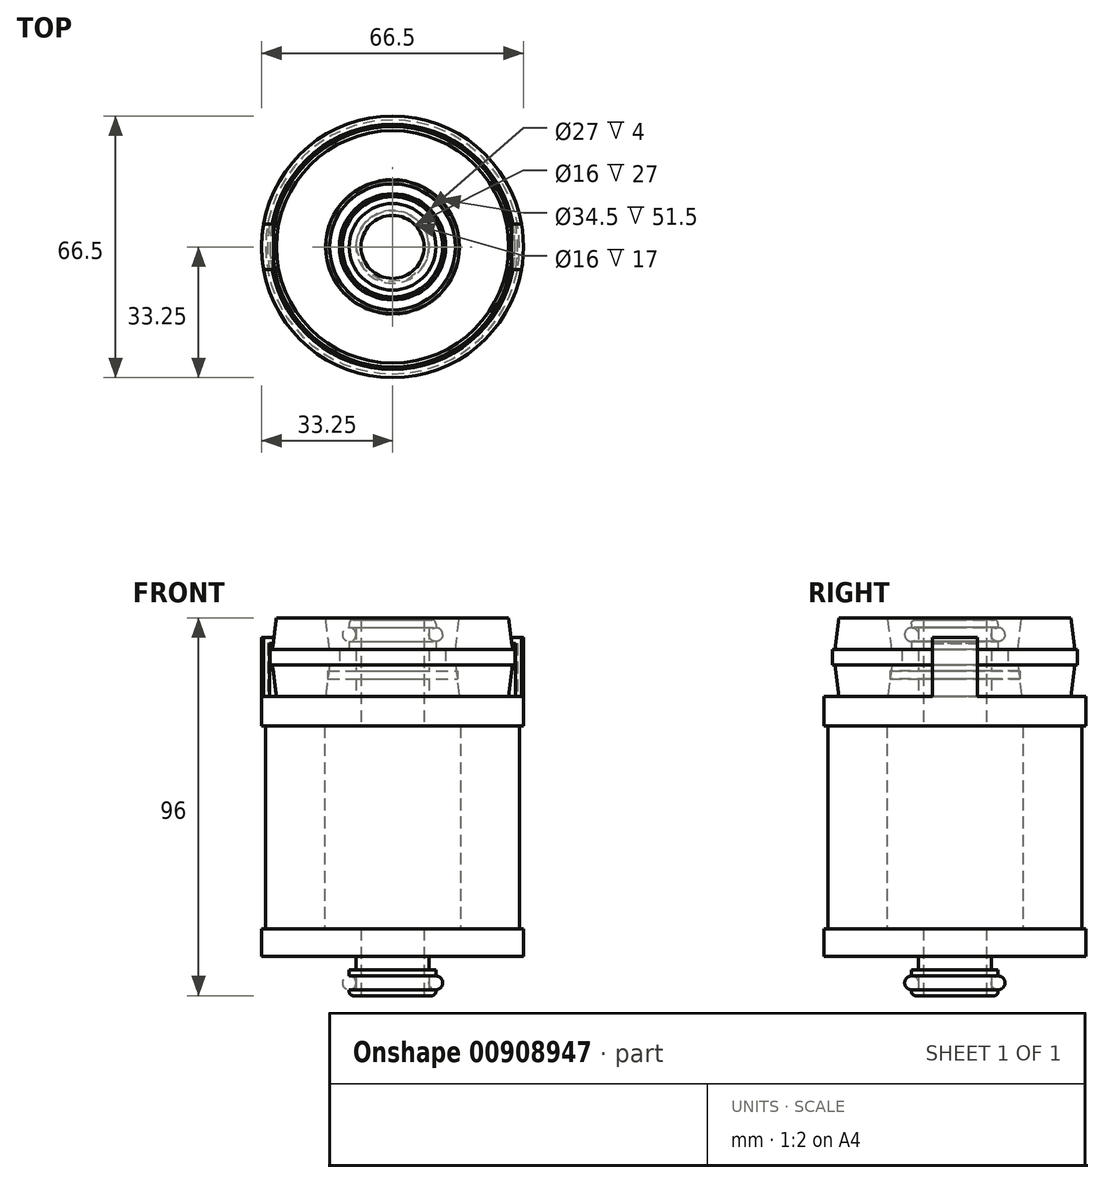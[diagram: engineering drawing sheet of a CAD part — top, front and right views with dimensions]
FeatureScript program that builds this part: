
annotation { "Feature Type Name" : "Feature", "Feature Type Description" : "" }
export const myFeature = defineFeature(function(context is Context, id is Id, definition is map)
    precondition{}
    {
        {
            var Q0;
            Q0=qCreatedBy(makeId("Front.planeOp"),FACE);
            var sketch = newSketch(context, id + "F0", { "sketchPlane" : qUnion([Q0])});
            skLineSegment(sketch, "E0", {"start": v(0, -41.92) * mm, "end": v(0, 59.56) * mm, "construction": true});
            skLineSegment(sketch, "E1", {"start": v(8, 0) * mm, "end": v(10, 0) * mm});
            skLineSegment(sketch, "E2", {"start": v(11, 1) * mm, "end": v(11, 1.5) * mm});
            skLineSegment(sketch, "E3", {"start": v(11, 1.5) * mm, "end": v(9.25, 1.5) * mm});
            skLineSegment(sketch, "E4", {"start": v(9.25, 1.5) * mm, "end": v(9.25, 5) * mm});
            skLineSegment(sketch, "E5", {"start": v(9.25, 5) * mm, "end": v(11, 5) * mm});
            skLineSegment(sketch, "E6", {"start": v(11, 5) * mm, "end": v(11, 6.5) * mm});
            skLineSegment(sketch, "E7", {"start": v(11, 6.5) * mm, "end": v(9.25, 6.5) * mm});
            skLineSegment(sketch, "E8", {"start": v(9.25, 6.5) * mm, "end": v(9.25, 10) * mm});
            skLineSegment(sketch, "E9", {"start": v(9.25, 10) * mm, "end": v(33.25, 10) * mm});
            skLineSegment(sketch, "E10", {"start": v(33.25, 10) * mm, "end": v(33.25, 17) * mm});
            skLineSegment(sketch, "E11", {"start": v(33.25, 76) * mm, "end": v(16.5, 76) * mm});
            skLineSegment(sketch, "E12", {"start": v(16.5, 80.5) * mm, "end": v(16.5, 82.5) * mm});
            skLineSegment(sketch, "E13", {"start": v(16.5, 82.5) * mm, "end": v(13.13, 82.5) * mm});
            skLineSegment(sketch, "E14", {"start": v(13.13, 82.5) * mm, "end": v(9.25, 82.5) * mm});
            skLineSegment(sketch, "E15", {"start": v(9.25, 82.5) * mm, "end": v(9.25, 88) * mm});
            skLineSegment(sketch, "E16", {"start": v(9.25, 88) * mm, "end": v(11, 88) * mm});
            skLineSegment(sketch, "E17", {"start": v(11, 88) * mm, "end": v(11, 90) * mm});
            skLineSegment(sketch, "E18", {"start": v(11, 90) * mm, "end": v(9.25, 90) * mm});
            skLineSegment(sketch, "E19", {"start": v(9.25, 90) * mm, "end": v(9.25, 93.5) * mm});
            skLineSegment(sketch, "E20", {"start": v(9.25, 93.5) * mm, "end": v(11, 93.5) * mm});
            skLineSegment(sketch, "E21", {"start": v(11, 93.5) * mm, "end": v(11, 94.5) * mm});
            skLineSegment(sketch, "E22", {"start": v(10, 95.5) * mm, "end": v(8, 95.5) * mm});
            skLineSegment(sketch, "E23", {"start": v(8, 95.5) * mm, "end": v(8, 68.5) * mm});
            skLineSegment(sketch, "E24", {"start": v(8, 68.5) * mm, "end": v(33.25, 68.5) * mm});
            skLineSegment(sketch, "E25", {"start": v(8, 0) * mm, "end": v(8, 17) * mm});
            skLineSegment(sketch, "E26", {"start": v(8, 17) * mm, "end": v(33.25, 17) * mm});
            skLineSegment(sketch, "E27", {"start": v(17.25, 17) * mm, "end": v(17.25, 68.5) * mm});
            skLineSegment(sketch, "E28", {"start": v(32.25, 68.5) * mm, "end": v(32.25, 17) * mm});
            skLineSegment(sketch, "E29.trimOffspring", {"start": v(33.25, 68.5) * mm, "end": v(33.25, 76) * mm});
            skLineSegment(sketch, "E30", {"start": v(16.5, 76) * mm, "end": v(9.25, 76) * mm});
            skLineSegment(sketch, "E31", {"start": v(9.25, 76) * mm, "end": v(9.25, 80.5) * mm});
            skLineSegment(sketch, "E32", {"start": v(9.25, 80.5) * mm, "end": v(16.5, 80.5) * mm});
            skPoint(sketch, "E33.visualSharp", {"position": v(11, 95.5) * mm});
            skArc(sketch, "E33.filletArc", {"start": v(11, 94.5) * mm, "mid": v(10.7, 95.2) * mm, "end": v(10, 95.5) * mm});
            skPoint(sketch, "E34.visualSharp", {"position": v(11, 0) * mm});
            skArc(sketch, "E34.filletArc", {"start": v(10, 0) * mm, "mid": v(10.7, 0.3) * mm, "end": v(11, 1) * mm});
            skSolve(sketch);
        }
        {
            var Q0;
            Q0 = qSketchRegion(id + "F0", true);
            var Q1;
            Q1=sQuery(id+"F0.wireOp",EDGE,"E0");
            revolve(context, id + "F1", {"surfaceOperationType" : NewSurfaceOperationType.NEW, "entities" : qUnion([Q0]), "axis" : qUnion([Q1]), "revolveType" : RevolveType.FULL});
        }
        {
            var Q0;
            Q0=qCreatedBy(makeId("Front.planeOp"),FACE);
            var sketch = newSketch(context, id + "F2", { "sketchPlane" : qUnion([Q0])});
            skLineSegment(sketch, "E35.0", {"start": v(11, 90) * mm, "end": v(9.25, 90) * mm, "construction": true});
            skLineSegment(sketch, "E35.1", {"start": v(9.25, 90) * mm, "end": v(9.25, 93.5) * mm, "construction": true});
            skLineSegment(sketch, "E35.2", {"start": v(9.25, 93.5) * mm, "end": v(11, 93.5) * mm, "construction": true});
            skCircle(sketch, "E36", {"center": v(11, 91.75) * mm, "radius": 1.75 * mm});
            skLineSegment(sketch, "E37.0", {"start": v(9.25, 5) * mm, "end": v(11, 5) * mm, "construction": true});
            skLineSegment(sketch, "E37.1", {"start": v(9.25, 1.5) * mm, "end": v(9.25, 5) * mm, "construction": true});
            skLineSegment(sketch, "E37.2", {"start": v(11, 1.5) * mm, "end": v(9.25, 1.5) * mm, "construction": true});
            skPoint(sketch, "E37.3", {"position": v(9.25, 3.25) * mm});
            skCircle(sketch, "E38", {"center": v(11, 3.25) * mm, "radius": 1.75 * mm});
            skSolve(sketch);
        }
        {
            var Q0;
            Q0 = qSketchRegion(id + "F2", true);
            var Q1;
            Q1=sQuery(id+"F0.wireOp",EDGE,"E0");
            revolve(context, id + "F3", {"surfaceOperationType" : NewSurfaceOperationType.NEW, "entities" : qUnion([Q0]), "axis" : qUnion([Q1]), "revolveType" : RevolveType.FULL});
        }
        {
            var Q0;
            Q0=makeQuery(id+"F1.opRevolve","SWEPT_FACE",FACE,{"disambiguationData":[OSD([sQuery(id+"F0.wireOp",EDGE,"E11"),sQuery(id+"F0.wireOp",EDGE,"E30")])]});
            var sketch = newSketch(context, id + "F4", { "sketchPlane" : qUnion([Q0])});
            skArc(sketch, "E39.0", {"start": v(32.75, -5.75) * mm, "mid": v(33.25, 0) * mm, "end": v(32.75, 5.75) * mm});
            skArc(sketch, "E40", {"start": v(31.22, -5.75) * mm, "mid": v(31.75, 0) * mm, "end": v(31.22, 5.75) * mm});
            skLineSegment(sketch, "E41", {"start": v(38.87, 0) * mm, "end": v(-40.84, 0) * mm, "construction": true});
            skLineSegment(sketch, "E42", {"start": v(-32.75, 5.75) * mm, "end": v(-31.22, 5.75) * mm});
            skLineSegment(sketch, "E43", {"start": v(32.75, -5.75) * mm, "end": v(31.22, -5.75) * mm});
            skLineSegment(sketch, "E44.trimOffspring", {"start": v(-31.22, -5.75) * mm, "end": v(-32.75, -5.75) * mm});
            skLineSegment(sketch, "E45.trimOffspring", {"start": v(31.22, 5.75) * mm, "end": v(32.75, 5.75) * mm});
            skArc(sketch, "E46.trimOffspring", {"start": v(-31.22, 5.75) * mm, "mid": v(-31.75, 0) * mm, "end": v(-31.22, -5.75) * mm});
            skArc(sketch, "E47.trimOffspring", {"start": v(-32.75, 5.75) * mm, "mid": v(-33.25, 0) * mm, "end": v(-32.75, -5.75) * mm});
            skSolve(sketch);
        }
        {
            var Q0;
            Q0 = qSketchRegion(id + "F4", true);
            extrude(context, id + "F5", {"entities" : qUnion([Q0]), "operationType" : NewBodyOperationType.ADD, "depth" : 13.5 * mm, "offsetDistance" : 25 * mm});
        }
        {
            var Q0;
            Q0=makeQuery(id+"F5.opExtrude","CAP_FACE",FACE,{"disambiguationData":[OSD([sQuery(id+"F4.wireOp",EDGE,"E39.0"),sQuery(id+"F4.wireOp",EDGE,"E40"),sQuery(id+"F4.wireOp",EDGE,"E43"),sQuery(id+"F4.wireOp",EDGE,"E45.trimOffspring")])],"isStart":false});
            var sketch = newSketch(context, id + "F6", { "sketchPlane" : qUnion([Q0])});
            skArc(sketch, "E48.0", {"start": v(32.75, 5.75) * mm, "mid": v(33.25, 0) * mm, "end": v(32.75, -5.75) * mm});
            skArc(sketch, "E48.1", {"start": v(-32.75, -5.75) * mm, "mid": v(-33.25, 0) * mm, "end": v(-32.75, 5.75) * mm});
            skLineSegment(sketch, "E49", {"start": v(-32.75, -5.75) * mm, "end": v(-30.25, -5.75) * mm});
            skLineSegment(sketch, "E50", {"start": v(-30.25, -5.75) * mm, "end": v(-30.25, 5.75) * mm});
            skLineSegment(sketch, "E51", {"start": v(-30.25, 5.75) * mm, "end": v(-32.75, 5.75) * mm});
            skLineSegment(sketch, "E52", {"start": v(32.75, -5.75) * mm, "end": v(30.25, -5.75) * mm});
            skLineSegment(sketch, "E53", {"start": v(30.25, -5.75) * mm, "end": v(30.25, 5.75) * mm});
            skLineSegment(sketch, "E54", {"start": v(30.25, 5.75) * mm, "end": v(32.75, 5.75) * mm});
            skSolve(sketch);
        }
        {
            var Q0;
            Q0 = qSketchRegion(id + "F6", true);
            extrude(context, id + "F7", {"entities" : qUnion([Q0]), "operationType" : NewBodyOperationType.ADD, "depth" : 1.5 * mm, "offsetDistance" : 25 * mm});
        }
        {
            var Q0;
            Q0=qCreatedBy(makeId("Front.planeOp"),FACE);
            var sketch = newSketch(context, id + "F8", { "sketchPlane" : qUnion([Q0])});
            skLineSegment(sketch, "E55.0", {"start": v(32.75, 76) * mm, "end": v(-32.75, 76) * mm, "construction": true});
            skLineSegment(sketch, "E56", {"start": v(-29.5, 76) * mm, "end": v(-17, 76) * mm});
            skLineSegment(sketch, "E57", {"start": v(-17, 76) * mm, "end": v(-16, 84) * mm});
            skLineSegment(sketch, "E58", {"start": v(-16, 84) * mm, "end": v(-13.5, 84) * mm});
            skLineSegment(sketch, "E59", {"start": v(-13.5, 84) * mm, "end": v(-13.5, 86) * mm});
            skLineSegment(sketch, "E60", {"start": v(-13.5, 86) * mm, "end": v(-31.14, 86) * mm});
            skLineSegment(sketch, "E61", {"start": v(-29.5, 76) * mm, "end": v(-30.5, 84) * mm});
            skLineSegment(sketch, "E62", {"start": v(-30.5, 84) * mm, "end": v(-31.14, 84) * mm});
            skLineSegment(sketch, "E63", {"start": v(-31.14, 84) * mm, "end": v(-31.14, 86) * mm});
            skLineSegment(sketch, "E64", {"start": v(0, 0) * mm, "end": v(0, 94.23) * mm, "construction": true});
            skPoint(sketch, "E64.endSnap0", {"position": v(0, 76) * mm});
            skLineSegment(sketch, "E65.MirrorCS", {"start": v(-16, 88) * mm, "end": v(-13.5, 88) * mm});
            skLineSegment(sketch, "E66.MirrorCS", {"start": v(-31.14, 88) * mm, "end": v(-31.14, 86) * mm});
            skLineSegment(sketch, "E67.MirrorCS", {"start": v(-30.5, 88) * mm, "end": v(-31.14, 88) * mm});
            skLineSegment(sketch, "E68.MirrorCS", {"start": v(-13.5, 88) * mm, "end": v(-13.5, 86) * mm});
            skLineSegment(sketch, "E69.MirrorCS", {"start": v(-17, 96) * mm, "end": v(-16, 88) * mm});
            skLineSegment(sketch, "E70.MirrorCS", {"start": v(-29.5, 96) * mm, "end": v(-17, 96) * mm});
            skLineSegment(sketch, "E71.MirrorCS", {"start": v(-29.5, 96) * mm, "end": v(-30.5, 88) * mm});
            skSolve(sketch);
        }
        {
            var Q0;
            Q0 = qSketchRegion(id + "F8", true);
            var Q1;
            Q1=sQuery(id+"F8.wireOp",EDGE,"E64");
            revolve(context, id + "F9", {"surfaceOperationType" : NewSurfaceOperationType.NEW, "entities" : qUnion([Q0]), "axis" : qUnion([Q1]), "revolveType" : RevolveType.FULL});
        }
    });
